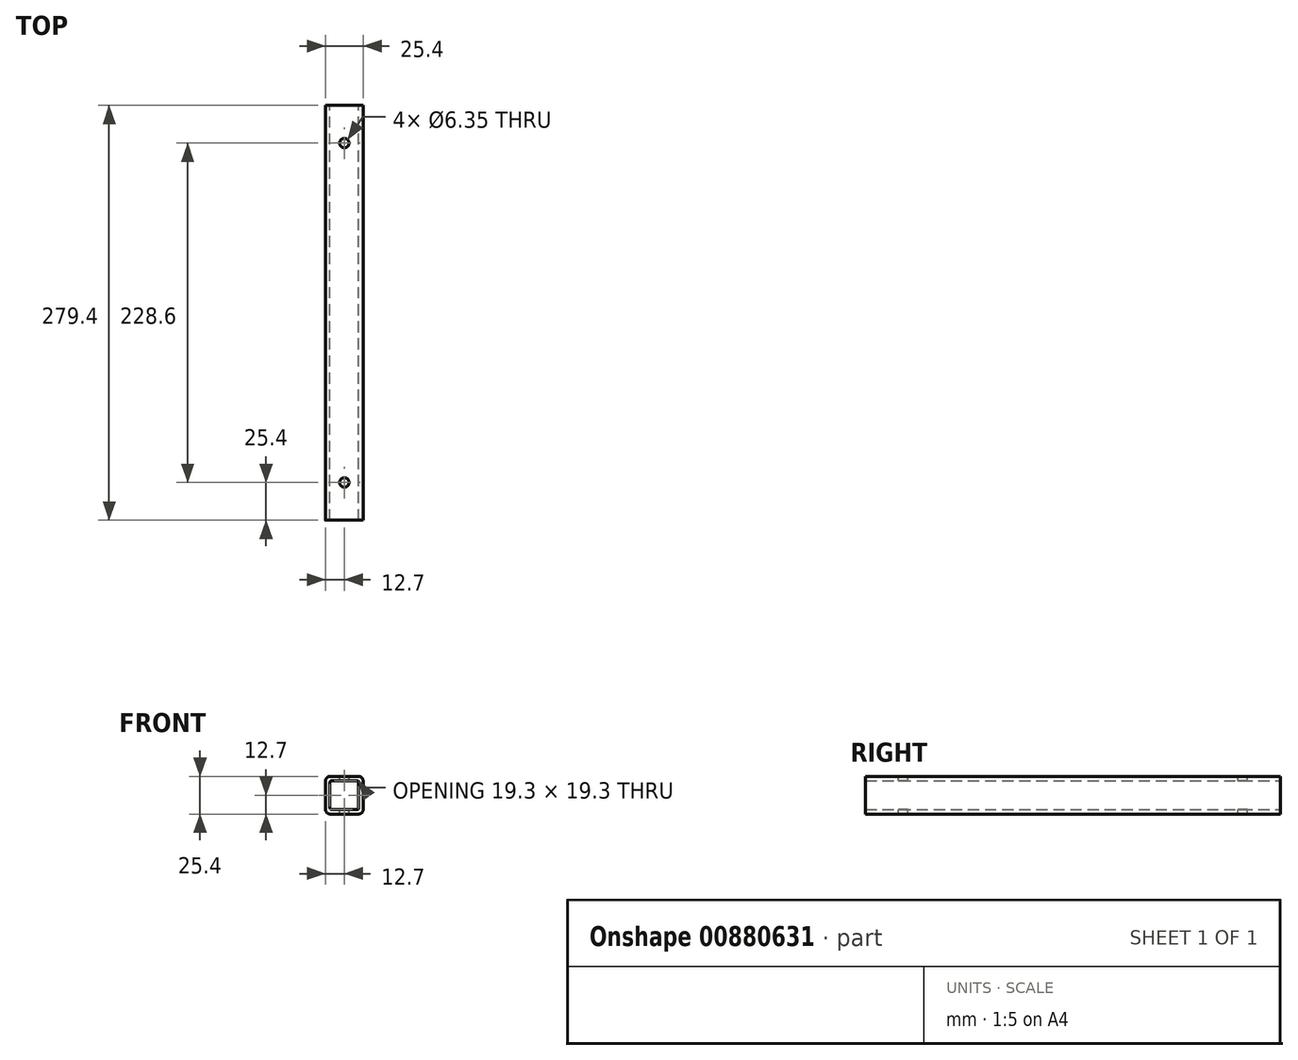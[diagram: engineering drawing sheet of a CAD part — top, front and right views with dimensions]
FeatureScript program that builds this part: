
annotation { "Feature Type Name" : "Feature", "Feature Type Description" : "" }
export const myFeature = defineFeature(function(context is Context, id is Id, definition is map)
    precondition{}
    {
        {
            var Q0;
            Q0=qCreatedBy(makeId("Front.planeOp"),FACE);
            var sketch = newSketch(context, id + "F0", { "sketchPlane" : qUnion([Q0])});
            skLineSegment(sketch, "E0.bottom", {"start": v(-9.52, 0) * mm, "end": v(9.52, 0) * mm});
            skLineSegment(sketch, "E0.top", {"start": v(-9.52, -25.4) * mm, "end": v(9.52, -25.4) * mm});
            skLineSegment(sketch, "E0.left", {"start": v(-12.7, -3.18) * mm, "end": v(-12.7, -22.22) * mm});
            skLineSegment(sketch, "E0.right", {"start": v(12.7, -3.17) * mm, "end": v(12.7, -22.22) * mm});
            skLineSegment(sketch, "E1.0", {"start": v(-8.64, -3.05) * mm, "end": v(8.64, -3.05) * mm});
            skLineSegment(sketch, "E1.1", {"start": v(-9.65, -4.06) * mm, "end": v(-9.65, -21.34) * mm});
            skLineSegment(sketch, "E1.2", {"start": v(-8.64, -22.35) * mm, "end": v(8.64, -22.35) * mm});
            skLineSegment(sketch, "E1.3", {"start": v(9.65, -4.06) * mm, "end": v(9.65, -21.34) * mm});
            skPoint(sketch, "E2.visualSharp", {"position": v(12.7, 0) * mm});
            skArc(sketch, "E2.filletArc", {"start": v(12.7, -3.17) * mm, "mid": v(11.77, -0.93) * mm, "end": v(9.52, 0) * mm});
            skPoint(sketch, "E3.visualSharp", {"position": v(12.7, -25.4) * mm});
            skArc(sketch, "E3.filletArc", {"start": v(9.52, -25.4) * mm, "mid": v(11.77, -24.47) * mm, "end": v(12.7, -22.22) * mm});
            skPoint(sketch, "E4.visualSharp", {"position": v(-12.7, -25.4) * mm});
            skArc(sketch, "E4.filletArc", {"start": v(-12.7, -22.22) * mm, "mid": v(-11.77, -24.47) * mm, "end": v(-9.52, -25.4) * mm});
            skPoint(sketch, "E5.visualSharp", {"position": v(-12.7, 0) * mm});
            skArc(sketch, "E5.filletArc", {"start": v(-9.53, 0) * mm, "mid": v(-11.77, -0.93) * mm, "end": v(-12.7, -3.18) * mm});
            skPoint(sketch, "E6.visualSharp", {"position": v(-9.65, -22.35) * mm});
            skArc(sketch, "E6.filletArc", {"start": v(-9.65, -21.34) * mm, "mid": v(-9.35, -22.05) * mm, "end": v(-8.64, -22.35) * mm});
            skPoint(sketch, "E7.visualSharp", {"position": v(9.65, -22.35) * mm});
            skArc(sketch, "E7.filletArc", {"start": v(8.64, -22.35) * mm, "mid": v(9.35, -22.05) * mm, "end": v(9.65, -21.34) * mm});
            skPoint(sketch, "E8.visualSharp", {"position": v(9.65, -3.05) * mm});
            skArc(sketch, "E8.filletArc", {"start": v(9.65, -4.06) * mm, "mid": v(9.35, -3.35) * mm, "end": v(8.64, -3.05) * mm});
            skPoint(sketch, "E9.visualSharp", {"position": v(-9.65, -3.05) * mm});
            skArc(sketch, "E9.filletArc", {"start": v(-8.64, -3.05) * mm, "mid": v(-9.35, -3.35) * mm, "end": v(-9.65, -4.06) * mm});
            skSolve(sketch);
        }
        {
            var Q0;
            Q0=qSketchRegion(id+"F0",true);
            extrude(context, id + "F1", {"entities" : qUnion([Q0]), "depth" : 279.4 * mm, "offsetDistance" : 25.4 * mm});
        }
        {
            var Q0;
            Q0=qCreatedBy(makeId("Top.planeOp"),FACE);
            var sketch = newSketch(context, id + "F2", { "sketchPlane" : qUnion([Q0])});
            skCircle(sketch, "E10", {"center": v(0, -25.4) * mm, "radius": 3.17 * mm});
            skCircle(sketch, "E11", {"center": v(0, -254) * mm, "radius": 3.18 * mm});
            skSolve(sketch);
        }
        {
            var Q0;
            Q0 = qSketchRegion(id + "F2", true);
            extrude(context, id + "F3", {"entities" : qUnion([Q0]), "operationType" : NewBodyOperationType.REMOVE, "oppositeDirection" : true, "depth" : 25.4 * mm, "offsetDistance" : 25.4 * mm});
        }
    });
